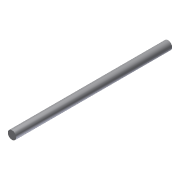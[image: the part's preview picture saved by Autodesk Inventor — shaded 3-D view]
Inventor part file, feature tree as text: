
AUTODESK INVENTOR PART (.ipt)
format: ipt  version: 2012 (Build 160160000, 160)  size: 65,536 bytes
history: native  units: in
note: dims shown in document units (in); Inventor stores cm internally (conversion verified against a paired STEP export)
features: extrude x1, sketch x1
ambient origin geometry x8: Origin, YZ Plane, XZ Plane, XY Plane, X Axis, Y Axis, Z Axis, Center Point
bodies: Solid1 (feature_tree)
feature tree (2):
  extrude  "Extrusion1"  Depth=7.0in TaperAngle=0.0deg
  sketch  "Sketch1"  dims[d0=0.375in d1=7.0in d2=0.0in]
